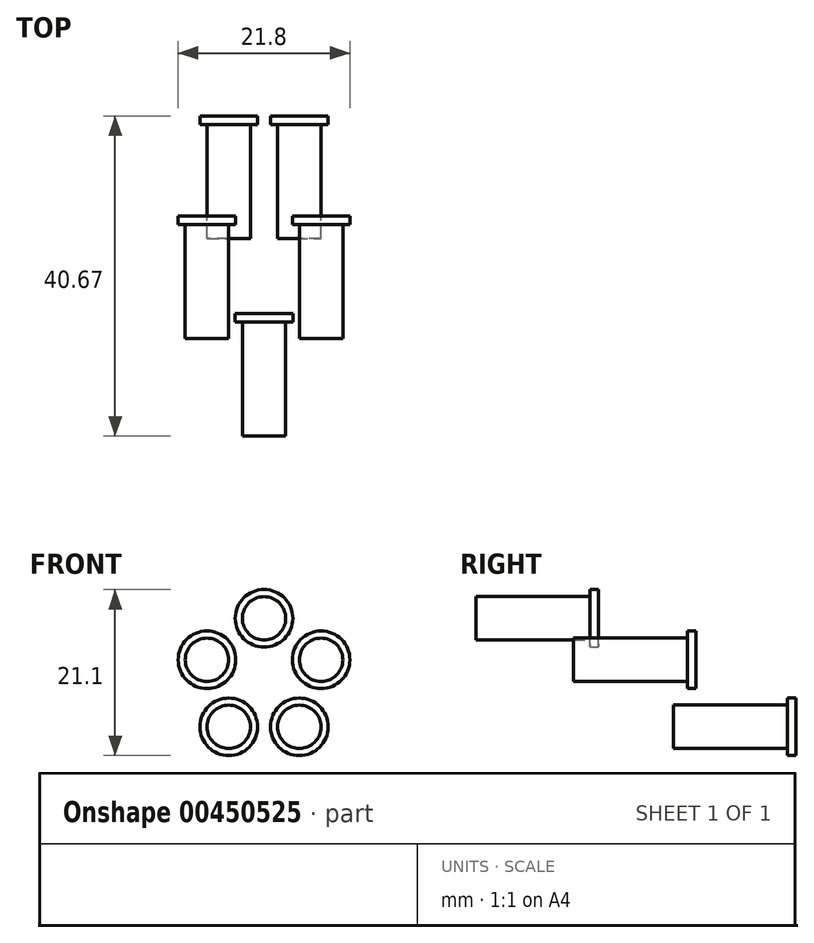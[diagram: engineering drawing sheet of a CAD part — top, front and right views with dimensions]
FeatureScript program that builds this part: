
annotation { "Feature Type Name" : "Feature", "Feature Type Description" : "" }
export const myFeature = defineFeature(function(context is Context, id is Id, definition is map)
    precondition{}
    {
        {
            var Q0;
            Q0=qCreatedBy(makeId("Front.planeOp"),FACE);
            var sketch = newSketch(context, id + "F0", { "sketchPlane" : qUnion([Q0])});
            skCircle(sketch, "E0", {"center": v(0, 7.62) * mm, "radius": 3.66 * mm});
            skCircle(sketch, "E1", {"center": v(0, 7.62) * mm, "radius": 2.76 * mm});
            skSolve(sketch);
        }
        {
            var Q0;
            Q0=makeQuery(id+"F0.imprint","IMPRINT",FACE,{"disambiguationData":[TD([[makeQuery(id+"F0.imprint","IMPRINT",EDGE,{"derivedFrom":sQuery(id+"F0.wireOp",EDGE,"E1")}),1.0]])]});
            extrude(context, id + "F1", {"entities" : qUnion([Q0]), "depth" : 15.57 * mm});
        }
        {
            var Q0;
            Q0=makeQuery(id+"F0.imprint","IMPRINT",FACE,{"disambiguationData":[TD([[makeQuery(id+"F0.imprint","IMPRINT",EDGE,{"derivedFrom":sQuery(id+"F0.wireOp",EDGE,"E0")}),1.0]])]});
            extrude(context, id + "F2", {"entities" : qUnion([Q0]), "operationType" : NewBodyOperationType.ADD, "depth" : 1.1 * mm});
        }
        {
            var Q0;
            Q0=qCreatedBy(makeId("Top.planeOp"),FACE);
            var sketch = newSketch(context, id + "F3", { "sketchPlane" : qUnion([Q0])});
            skLineSegment(sketch, "E2", {"start": v(0, 0) * mm, "end": v(0, -25.4) * mm});
            skSolve(sketch);
        }
        {
            var Q0;
            Q0=makeQuery(id+"F1.opExtrude","SWEPT_BODY",BODY,{"disambiguationData":[OSD([sQuery(id+"F0.wireOp",EDGE,"E1")])]});
            var Q1;
            Q1=sQuery(id+"F3.wireOp",EDGE,"E2");
            circularPattern(context, id + "F4", {"entities" : qUnion([Q0]), "axis" : qUnion([Q1]), "angle" : 360 * degree, "instanceCount" : 5, "equalSpace" : true, "computeTransformsWithoutBuiltin" : true});
        }
        {
            var Q0;
            Q0=makeQuery(id+"F4.opPattern","COPY",BODY,{"derivedFrom":makeQuery(id+"F1.opExtrude","SWEPT_BODY",BODY,{"disambiguationData":[OSD([sQuery(id+"F0.wireOp",EDGE,"E1")])]}),"instanceName":"1"});
            var Q1;
            Q1=makeQuery(id+"F4.opPattern","COPY",BODY,{"derivedFrom":makeQuery(id+"F1.opExtrude","SWEPT_BODY",BODY,{"disambiguationData":[OSD([sQuery(id+"F0.wireOp",EDGE,"E1")])]}),"instanceName":"4"});
            transform(context, id + "F5", {"entities" : qUnion([Q0, Q1]), "transformType" : TransformType.TRANSLATION_3D, "dx" : 0 * mm, "dy" : 12.4 * mm, "dz" : 0 * mm, "makeCopy" : false});
        }
        {
            var Q0;
            Q0=makeQuery(id+"F4.opPattern","COPY",BODY,{"derivedFrom":makeQuery(id+"F1.opExtrude","SWEPT_BODY",BODY,{"disambiguationData":[OSD([sQuery(id+"F0.wireOp",EDGE,"E1")])]}),"instanceName":"2"});
            var Q1;
            Q1=makeQuery(id+"F4.opPattern","COPY",BODY,{"derivedFrom":makeQuery(id+"F1.opExtrude","SWEPT_BODY",BODY,{"disambiguationData":[OSD([sQuery(id+"F0.wireOp",EDGE,"E1")])]}),"instanceName":"3"});
            transform(context, id + "F6", {"entities" : qUnion([Q0, Q1]), "transformType" : TransformType.TRANSLATION_3D, "dx" : 0 * mm, "dy" : 25.1 * mm, "dz" : 0 * mm, "makeCopy" : false});
        }
    });
